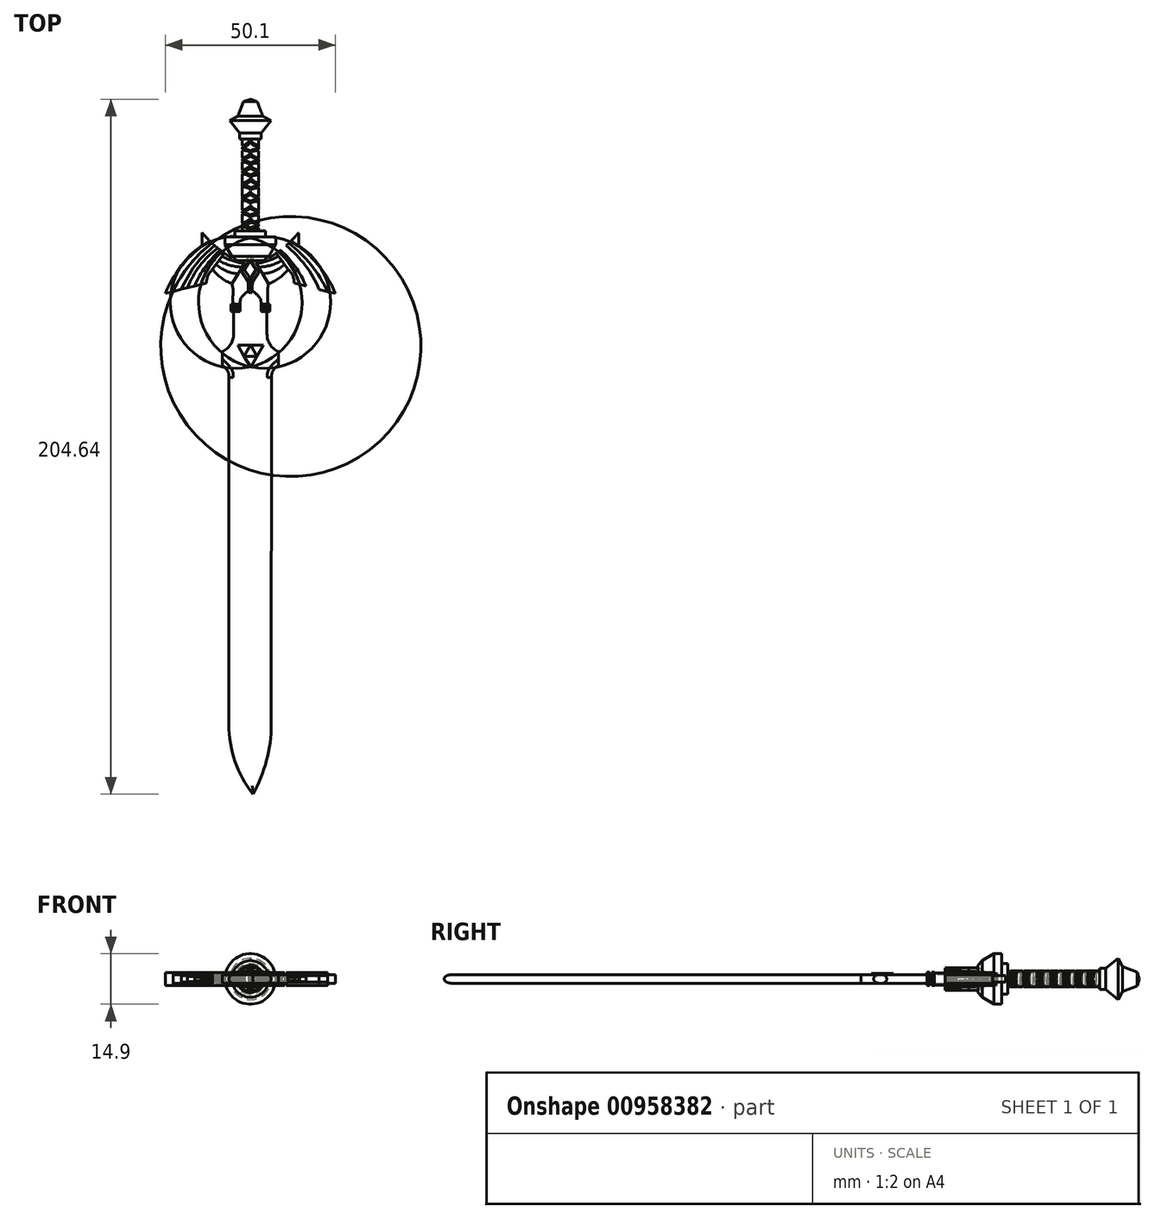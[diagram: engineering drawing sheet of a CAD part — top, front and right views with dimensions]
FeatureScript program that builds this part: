
annotation { "Feature Type Name" : "Feature", "Feature Type Description" : "" }
export const myFeature = defineFeature(function(context is Context, id is Id, definition is map)
    precondition{}
    {
        {
            var Q0;
            Q0=qCreatedBy(makeId("Top.planeOp"),FACE);
            var sketch = newSketch(context, id + "F0", { "sketchPlane" : qUnion([Q0])});
            skLineSegment(sketch, "E0", {"start": v(-5.22, 76.34) * mm, "end": v(-7.23, 75.61) * mm});
            skLineSegment(sketch, "E1", {"start": v(-7.23, 75.61) * mm, "end": v(-8.9, 71.32) * mm});
            skLineSegment(sketch, "E2", {"start": v(-8.9, 71.32) * mm, "end": v(-11.32, 70.05) * mm});
            skLineSegment(sketch, "E3", {"start": v(-11.32, 70.05) * mm, "end": v(-8.36, 66.38) * mm});
            skLineSegment(sketch, "E4", {"start": v(-8.36, 66.38) * mm, "end": v(-8.36, 64.56) * mm});
            skLineSegment(sketch, "E5", {"start": v(-8.36, 64.56) * mm, "end": v(-7.6, 64.56) * mm});
            skLineSegment(sketch, "E6", {"start": v(-7.6, 64.56) * mm, "end": v(-7.6, 37.58) * mm});
            skLineSegment(sketch, "E7", {"start": v(-7.6, 37.58) * mm, "end": v(-9.75, 37.58) * mm});
            skLineSegment(sketch, "E8", {"start": v(-9.75, 37.58) * mm, "end": v(-9.75, 35.78) * mm});
            skLineSegment(sketch, "E9", {"start": v(-9.75, 35.78) * mm, "end": v(-12.69, 35.78) * mm});
            skLineSegment(sketch, "E10", {"start": v(-12.69, 35.78) * mm, "end": v(-12.69, 33.54) * mm});
            skLineSegment(sketch, "E11", {"start": v(-12.69, 33.54) * mm, "end": v(-10.65, 30.07) * mm});
            skLineSegment(sketch, "E12", {"start": v(-10.65, 30.07) * mm, "end": v(-9.23, 28.83) * mm});
            skLineSegment(sketch, "E13", {"start": v(-9.23, 28.83) * mm, "end": v(-6.85, 28.22) * mm});
            skLineSegment(sketch, "E14", {"start": v(-6.85, 28.22) * mm, "end": v(-5.24, 30.4) * mm});
            skLineSegment(sketch, "E15", {"start": v(-5.24, 30.4) * mm, "end": v(-5.22, 76.34) * mm});
            skLineSegment(sketch, "E16", {"start": v(-10.65, 30.07) * mm, "end": v(-10.65, 29.62) * mm});
            skPoint(sketch, "E17.1.internal.snap0", {"position": v(-11.67, 31.8) * mm});
            skFitSpline(sketch, "E17", {"points": [v(-10.65, 29.62) * mm, v(-11.67, 30.16) * mm, v(-14.84, 32.47) * mm, v(-17.18, 34.56) * mm, v(-19.44, 37) * mm], "startDerivative": vector(-5.37, 2.5) * mm, "endDerivative": vector(-8.35, 9.25) * mm});
            skFitSpline(sketch, "E18", {"points": [v(-19.44, 37) * mm, v(-19.44, 35.95) * mm, v(-19.44, 33.83) * mm, v(-19.4, 33.07) * mm, v(-19.44, 33.1) * mm], "startDerivative": vector(0.06, -3.26) * mm, "endDerivative": vector(-1.19, 0.34) * mm});
            skArc(sketch, "E19", {"start": v(-19.4, 33.07) * mm, "mid": v(-25.78, 26.83) * mm, "end": v(-30.3, 19.12) * mm});
            skLineSegment(sketch, "E20", {"start": v(-30.3, 19.12) * mm, "end": v(-18.17, 22.24) * mm});
            skArc(sketch, "E21", {"start": v(-16.35, 26.26) * mm, "mid": v(-17.68, 24.44) * mm, "end": v(-18.17, 22.24) * mm});
            skArc(sketch, "E22", {"start": v(-16.35, 26.26) * mm, "mid": v(-13.8, 23.71) * mm, "end": v(-10.63, 21.98) * mm});
            skArc(sketch, "E23", {"start": v(-16.56, 33.95) * mm, "mid": v(-23.15, 27.52) * mm, "end": v(-28.02, 19.7) * mm});
            skArc(sketch, "E24", {"start": v(-15.75, 33.22) * mm, "mid": v(-21.45, 27.4) * mm, "end": v(-25.51, 20.35) * mm});
            skArc(sketch, "E25", {"start": v(-14.84, 32.47) * mm, "mid": v(-20.11, 27.25) * mm, "end": v(-23.78, 20.8) * mm});
            skArc(sketch, "E26", {"start": v(-14.1, 31.89) * mm, "mid": v(-18.47, 27.05) * mm, "end": v(-21.62, 21.35) * mm});
            skArc(sketch, "E27", {"start": v(-13.5, 31.43) * mm, "mid": v(-17.34, 27.1) * mm, "end": v(-19.75, 21.83) * mm});
            skLineSegment(sketch, "E28", {"start": v(-16.35, 26.26) * mm, "end": v(-12.92, 31) * mm});
            skLineSegment(sketch, "E29", {"start": v(-19.4, 33.07) * mm, "end": v(-17.18, 34.56) * mm});
            skArc(sketch, "E30", {"start": v(-15.35, 27.65) * mm, "mid": v(-12.5, 25.83) * mm, "end": v(-9.23, 24.95) * mm});
            skArc(sketch, "E31", {"start": v(-14.49, 28.83) * mm, "mid": v(-11.25, 27.44) * mm, "end": v(-7.76, 26.93) * mm});
            skArc(sketch, "E32", {"start": v(-13.57, 30.1) * mm, "mid": v(-10.47, 28.76) * mm, "end": v(-7.17, 28) * mm});
            skLineSegment(sketch, "E33", {"start": v(-6.85, 28.22) * mm, "end": v(-10.63, 21.98) * mm});
            skFitSpline(sketch, "E34", {"points": [v(-9.23, 24.95) * mm, v(-8.83, 24.95) * mm], "startDerivative": vector(0.4, 0) * mm, "endDerivative": vector(0.4, 0) * mm});
            skFitSpline(sketch, "E35", {"points": [v(-7.76, 26.93) * mm, v(-7.63, 26.93) * mm], "startDerivative": vector(0.13, 0) * mm, "endDerivative": vector(0.13, 0) * mm});
            skFitSpline(sketch, "E36", {"points": [v(-7.17, 28) * mm, v(-7, 27.99) * mm], "startDerivative": vector(0.17, -0.02) * mm, "endDerivative": vector(0.17, -0.02) * mm});
            skFitSpline(sketch, "E37.MirrorCS", {"points": [v(8.96, 36.98) * mm, v(8.96, 35.93) * mm, v(8.96, 33.81) * mm, v(8.9, 33.06) * mm, v(8.96, 33.08) * mm], "startDerivative": vector(-0.07, -3.26) * mm, "endDerivative": vector(1.19, 0.34) * mm});
            skLineSegment(sketch, "E38.MirrorCS", {"start": v(8.9, 33.06) * mm, "end": v(6.7, 34.54) * mm});
            skLineSegment(sketch, "E39.MirrorCS", {"start": v(5.86, 26.25) * mm, "end": v(2.43, 31) * mm});
            skLineSegment(sketch, "E40.MirrorCS", {"start": v(2.2, 35.77) * mm, "end": v(2.2, 33.53) * mm});
            skPoint(sketch, "E41.MirrorP", {"position": v(1.18, 31.8) * mm});
            skArc(sketch, "E42.MirrorCS", {"start": v(3.62, 31.88) * mm, "mid": v(7.97, 27.04) * mm, "end": v(11.12, 21.33) * mm});
            skArc(sketch, "E43.MirrorCS", {"start": v(5.27, 33.2) * mm, "mid": v(10.96, 27.4) * mm, "end": v(15.01, 20.33) * mm});
            skArc(sketch, "E44.MirrorCS", {"start": v(5.86, 26.25) * mm, "mid": v(7.18, 24.42) * mm, "end": v(7.67, 22.22) * mm});
            skArc(sketch, "E45.MirrorCS", {"start": v(4.36, 32.46) * mm, "mid": v(9.62, 27.23) * mm, "end": v(13.28, 20.78) * mm});
            skArc(sketch, "E46.MirrorCS", {"start": v(3, 31.42) * mm, "mid": v(6.85, 27.09) * mm, "end": v(9.25, 21.82) * mm});
            skLineSegment(sketch, "E47.MirrorCS", {"start": v(0.16, 30.07) * mm, "end": v(0.16, 29.61) * mm});
            skFitSpline(sketch, "E48.MirrorCS", {"points": [v(0.16, 29.61) * mm, v(1.18, 30.15) * mm, v(4.36, 32.46) * mm, v(6.7, 34.54) * mm, v(8.96, 36.98) * mm], "startDerivative": vector(5.37, 2.5) * mm, "endDerivative": vector(8.36, 9.24) * mm});
            skLineSegment(sketch, "E49.MirrorCS", {"start": v(2.2, 33.53) * mm, "end": v(0.16, 30.07) * mm});
            skArc(sketch, "E50.MirrorCS", {"start": v(5.86, 26.25) * mm, "mid": v(3.3, 23.7) * mm, "end": v(0.14, 21.97) * mm});
            skArc(sketch, "E51.MirrorCS", {"start": v(6.07, 33.93) * mm, "mid": v(12.66, 27.5) * mm, "end": v(17.52, 19.68) * mm});
            skArc(sketch, "E52.MirrorCS", {"start": v(8.9, 33.06) * mm, "mid": v(15.29, 26.8) * mm, "end": v(19.8, 19.1) * mm});
            skLineSegment(sketch, "E53.MirrorCS", {"start": v(19.8, 19.1) * mm, "end": v(7.67, 22.22) * mm});
            skFitSpline(sketch, "E54.MirrorCS", {"points": [v(0.16, 29.61) * mm, v(1.18, 30.15) * mm, v(4.36, 32.46) * mm, v(6.7, 34.54) * mm, v(8.96, 36.98) * mm], "startDerivative": vector(5.37, 2.5) * mm, "endDerivative": vector(8.36, 9.24) * mm});
            skArc(sketch, "E55.MirrorCS", {"start": v(4.86, 27.64) * mm, "mid": v(2, 25.82) * mm, "end": v(-1.27, 24.95) * mm});
            skArc(sketch, "E56.MirrorCS", {"start": v(4, 28.82) * mm, "mid": v(0.76, 27.43) * mm, "end": v(-2.73, 26.93) * mm});
            skArc(sketch, "E57.MirrorCS", {"start": v(3.08, 30.1) * mm, "mid": v(-0.02, 28.75) * mm, "end": v(-3.32, 28) * mm});
            skLineSegment(sketch, "E58.MirrorCS", {"start": v(-3.64, 28.22) * mm, "end": v(0.14, 21.97) * mm});
            skLineSegment(sketch, "E59.MirrorCS", {"start": v(0.16, 30.07) * mm, "end": v(-1.26, 28.83) * mm});
            skLineSegment(sketch, "E60.MirrorCS", {"start": v(-1.26, 28.83) * mm, "end": v(-3.64, 28.22) * mm});
            skFitSpline(sketch, "E61.MirrorCS", {"points": [v(-3.32, 28) * mm, v(-3.5, 27.99) * mm], "startDerivative": vector(-0.17, -0.02) * mm, "endDerivative": vector(-0.17, -0.02) * mm});
            skFitSpline(sketch, "E62.MirrorCS", {"points": [v(-2.73, 26.93) * mm, v(-2.86, 26.93) * mm], "startDerivative": vector(-0.13, 0) * mm, "endDerivative": vector(-0.13, 0) * mm});
            skFitSpline(sketch, "E63.MirrorCS", {"points": [v(-1.27, 24.95) * mm, v(-1.66, 24.95) * mm], "startDerivative": vector(-0.4, 0) * mm, "endDerivative": vector(-0.4, 0) * mm});
            skFitSpline(sketch, "E64", {"points": [v(-10.63, 21.98) * mm, v(-10.33, 20.1) * mm, v(-10.37, 18.46) * mm, v(-10.37, 16.67) * mm, v(-10.36, 15.95) * mm], "startDerivative": vector(1.43, -6.77) * mm, "endDerivative": vector(0.02, -3.56) * mm});
            skLineSegment(sketch, "E65", {"start": v(-10.36, 15.95) * mm, "end": v(-8.26, 15.95) * mm});
            skFitSpline(sketch, "E66", {"points": [v(-8.26, 15.95) * mm, v(-8.26, 16.44) * mm, v(-8.13, 17.45) * mm, v(-7.66, 18.2) * mm, v(-6.66, 19.28) * mm, v(-6, 19.75) * mm, v(-5.8, 19.83) * mm], "startDerivative": vector(-0.06, 3.2) * mm, "endDerivative": vector(1.98, 0.65) * mm});
            skFitSpline(sketch, "E67", {"points": [v(-4.62, 19.83) * mm, v(-3.94, 19.37) * mm, v(-3.02, 18.52) * mm, v(-2.42, 17.82) * mm, v(-2.16, 17.16) * mm, v(-2.1, 16.47) * mm, v(-2.1, 15.95) * mm], "startDerivative": vector(3.91, -2.38) * mm, "endDerivative": vector(0.1, -3.68) * mm});
            skLineSegment(sketch, "E68", {"start": v(-2.1, 15.95) * mm, "end": v(-0.16, 15.95) * mm});
            skFitSpline(sketch, "E69.MirrorCS", {"points": [v(0.14, 21.97) * mm, v(-0.17, 20.1) * mm, v(-0.13, 18.46) * mm, v(-0.13, 16.66) * mm, v(-0.14, 15.95) * mm], "startDerivative": vector(-1.44, -6.76) * mm, "endDerivative": vector(-0.02, -3.56) * mm});
            skLineSegment(sketch, "E70", {"start": v(-0.16, 15.95) * mm, "end": v(-0.14, 15.95) * mm});
            skLineSegment(sketch, "E71", {"start": v(-3.64, 28.22) * mm, "end": v(-5.24, 30.4) * mm});
            skLineSegment(sketch, "E72", {"start": v(-8.15, 26.08) * mm, "end": v(-5.86, 22.58) * mm});
            skLineSegment(sketch, "E73", {"start": v(-5.86, 22.58) * mm, "end": v(-5.8, 19.83) * mm});
            skLineSegment(sketch, "E74.MirrorCS", {"start": v(-2.34, 26.08) * mm, "end": v(-4.63, 22.58) * mm});
            skLineSegment(sketch, "E75.MirrorCS", {"start": v(-4.63, 22.58) * mm, "end": v(-4.7, 19.83) * mm});
            skLineSegment(sketch, "E76", {"start": v(-4.7, 19.83) * mm, "end": v(-4.62, 19.83) * mm});
            skLineSegment(sketch, "E77", {"start": v(-10.36, 15.95) * mm, "end": v(-10.95, 15.95) * mm});
            skLineSegment(sketch, "E78", {"start": v(-10.95, 15.95) * mm, "end": v(-10.95, 13.83) * mm});
            skLineSegment(sketch, "E79", {"start": v(-10.95, 13.83) * mm, "end": v(-8.63, 13.83) * mm});
            skLineSegment(sketch, "E80", {"start": v(-8.63, 13.83) * mm, "end": v(-8.27, 13.83) * mm});
            skLineSegment(sketch, "E81", {"start": v(-8.27, 13.83) * mm, "end": v(-8.26, 15.95) * mm});
            skLineSegment(sketch, "E82", {"start": v(-2.1, 15.95) * mm, "end": v(-2.1, 13.83) * mm});
            skLineSegment(sketch, "E83", {"start": v(-2.1, 13.83) * mm, "end": v(0.52, 13.83) * mm});
            skLineSegment(sketch, "E84", {"start": v(0.52, 13.83) * mm, "end": v(0.52, 15.95) * mm});
            skLineSegment(sketch, "E85", {"start": v(0.52, 15.95) * mm, "end": v(-0.16, 15.95) * mm});
            skLineSegment(sketch, "E86", {"start": v(-10.95, 15.26) * mm, "end": v(-8.26, 15.26) * mm});
            skLineSegment(sketch, "E87", {"start": v(-10.95, 14.53) * mm, "end": v(-8.26, 14.53) * mm});
            skLineSegment(sketch, "E88", {"start": v(-2.1, 15.22) * mm, "end": v(0.52, 15.22) * mm});
            skLineSegment(sketch, "E89", {"start": v(-2.1, 14.56) * mm, "end": v(0.52, 14.56) * mm});
            skLineSegment(sketch, "E90", {"start": v(-10.16, 13.83) * mm, "end": v(-10.16, 7.22) * mm});
            skArc(sketch, "E91", {"start": v(-13.54, 1.97) * mm, "mid": v(-11.08, 4.1) * mm, "end": v(-10.16, 7.22) * mm});
            skLineSegment(sketch, "E92", {"start": v(-13.54, 1.97) * mm, "end": v(-13.54, -1.9) * mm});
            skFitSpline(sketch, "E93", {"points": [v(-13.54, -1.9) * mm, v(-12.3, -3.14) * mm, v(-11.8, -3.88) * mm, v(-11.55, -4.81) * mm, v(-11.55, -5.66) * mm], "startDerivative": vector(4.34, -4.17) * mm, "endDerivative": vector(-0.22, -3.77) * mm});
            skLineSegment(sketch, "E94", {"start": v(-11.55, -5.66) * mm, "end": v(-11.55, -107.82) * mm});
            skLineSegment(sketch, "E95.MirrorCS", {"start": v(1.02, -5.67) * mm, "end": v(0.91, -107.82) * mm});
            skLineSegment(sketch, "E96.MirrorCS", {"start": v(-0.34, 13.83) * mm, "end": v(-0.35, 7.21) * mm});
            skArc(sketch, "E97.MirrorCS", {"start": v(3.03, 1.96) * mm, "mid": v(0.56, 4.1) * mm, "end": v(-0.35, 7.21) * mm});
            skLineSegment(sketch, "E98.MirrorCS", {"start": v(3.03, 1.96) * mm, "end": v(3.02, -1.91) * mm});
            skFitSpline(sketch, "E99.MirrorCS", {"points": [v(3.02, -1.91) * mm, v(1.78, -3.15) * mm, v(1.28, -3.9) * mm, v(1.02, -4.82) * mm, v(1.02, -5.67) * mm], "startDerivative": vector(-4.35, -4.17) * mm, "endDerivative": vector(0.22, -3.77) * mm});
            skArc(sketch, "E100", {"start": v(-11.55, -107.82) * mm, "mid": v(-9.73, -118.65) * mm, "end": v(-4.5, -128.3) * mm});
            skArc(sketch, "E101", {"start": v(-4.5, -128.3) * mm, "mid": v(-0.47, -118.4) * mm, "end": v(0.91, -107.82) * mm});
            skLineSegment(sketch, "E102", {"start": v(-4.7, 19.83) * mm, "end": v(-5.24, 19.13) * mm});
            skLineSegment(sketch, "E103", {"start": v(-5.24, 19.13) * mm, "end": v(-5.8, 19.83) * mm});
            skLineSegment(sketch, "E104", {"start": v(-0.34, 13.83) * mm, "end": v(-0.34, 13.83) * mm});
            skSolve(sketch);
        }
        {
            var Q0;
            Q0=makeQuery(id+"F0.imprint","IMPRINT",FACE,{"disambiguationData":[TD([[makeQuery(id+"F0.imprint","IMPRINT",EDGE,{"derivedFrom":sQuery(id+"F0.wireOp",EDGE,"E0")}),1.0]])]});
            var Q1;
            Q1=sQuery(id+"F0.wireOp",EDGE,"E15");
            revolve(context, id + "F1", {"surfaceOperationType" : NewSurfaceOperationType.NEW, "entities" : qUnion([Q0]), "axis" : qUnion([Q1]), "revolveType" : RevolveType.FULL});
        }
        {
            var Q0;
            {var subQ1=sQuery(id+"F0.wireOp",EDGE,"E22");Q0=makeQuery(id+"F0.imprint","IMPRINT",FACE,{"disambiguationData":[TD([[makeQuery(id+"F0.imprint","IMPRINT",EDGE,{"derivedFrom":subQ1}),1.0]])]});}
            var Q1;
            {var subQ2=sQuery(id+"F0.wireOp",EDGE,"E19");Q1=makeQuery(id+"F0.imprint","IMPRINT",FACE,{"disambiguationData":[TD([[makeQuery(id+"F0.imprint","IMPRINT",EDGE,{"derivedFrom":subQ2}),1.0]])]});}
            var Q2;
            {var subQ3=sQuery(id+"F0.wireOp",EDGE,"E55.MirrorCS");Q2=makeQuery(id+"F0.imprint","IMPRINT",FACE,{"disambiguationData":[TD([[makeQuery(id+"F0.imprint","IMPRINT",EDGE,{"derivedFrom":subQ3}),1.0]])]});}
            var Q3;
            {var subQ5=sQuery(id+"F0.wireOp",EDGE,"E51.MirrorCS");Q3=makeQuery(id+"F0.imprint","IMPRINT",FACE,{"disambiguationData":[TD([[makeQuery(id+"F0.imprint","IMPRINT",EDGE,{"derivedFrom":subQ5}),1.0]])]});}
            extrude(context, id + "F2", {"entities" : qUnion([Q0, Q1, Q2, Q3]), "endBound" : BoundingType.SYMMETRIC, "depth" : 3.86 * mm, "offsetDistance" : 25.4 * mm});
        }
        {
            var Q0;
            {var subQ0=sQuery(id+"F0.wireOp",EDGE,"E23");Q0=makeQuery(id+"F0.imprint","IMPRINT",FACE,{"disambiguationData":[TD([[makeQuery(id+"F0.imprint","IMPRINT",EDGE,{"derivedFrom":subQ0}),1.0]])]});}
            var Q1;
            {var subQ4=sQuery(id+"F0.wireOp",EDGE,"E30");Q1=makeQuery(id+"F0.imprint","IMPRINT",FACE,{"disambiguationData":[TD([[makeQuery(id+"F0.imprint","IMPRINT",EDGE,{"derivedFrom":subQ4}),1.0]])]});}
            var Q2;
            {var subQ3=sQuery(id+"F0.wireOp",EDGE,"E55.MirrorCS");Q2=makeQuery(id+"F0.imprint","IMPRINT",FACE,{"disambiguationData":[TD([[makeQuery(id+"F0.imprint","IMPRINT",EDGE,{"derivedFrom":subQ3}),-1.0]])]});}
            var Q3;
            {var subQ0=sQuery(id+"F0.wireOp",EDGE,"E51.MirrorCS");Q3=makeQuery(id+"F0.imprint","IMPRINT",FACE,{"disambiguationData":[TD([[makeQuery(id+"F0.imprint","IMPRINT",EDGE,{"derivedFrom":subQ0}),-1.0]])]});}
            extrude(context, id + "F3", {"entities" : qUnion([Q0, Q1, Q2, Q3]), "endBound" : BoundingType.SYMMETRIC, "depth" : 2.54 * mm, "offsetDistance" : 25.4 * mm});
        }
        {
            var Q0;
            {var subQ0=sQuery(id+"F0.wireOp",EDGE,"E24");Q0=makeQuery(id+"F0.imprint","IMPRINT",FACE,{"disambiguationData":[TD([[makeQuery(id+"F0.imprint","IMPRINT",EDGE,{"derivedFrom":subQ0}),1.0]])]});}
            var Q1;
            {var subQ4=sQuery(id+"F0.wireOp",EDGE,"E31");Q1=makeQuery(id+"F0.imprint","IMPRINT",FACE,{"disambiguationData":[TD([[makeQuery(id+"F0.imprint","IMPRINT",EDGE,{"derivedFrom":subQ4}),1.0]])]});}
            var Q2;
            {var subQ0=sQuery(id+"F0.wireOp",EDGE,"E43.MirrorCS");Q2=makeQuery(id+"F0.imprint","IMPRINT",FACE,{"disambiguationData":[TD([[makeQuery(id+"F0.imprint","IMPRINT",EDGE,{"derivedFrom":subQ0}),-1.0]])]});}
            var Q3;
            {var subQ3=sQuery(id+"F0.wireOp",EDGE,"E56.MirrorCS");Q3=makeQuery(id+"F0.imprint","IMPRINT",FACE,{"disambiguationData":[TD([[makeQuery(id+"F0.imprint","IMPRINT",EDGE,{"derivedFrom":subQ3}),-1.0]])]});}
            extrude(context, id + "F4", {"entities" : qUnion([Q0, Q1, Q2, Q3]), "endBound" : BoundingType.SYMMETRIC, "depth" : 1.93 * mm, "offsetDistance" : 25.4 * mm});
        }
        {
            var Q0;
            Q0=makeQuery(id+"F0.imprint","IMPRINT",FACE,{"disambiguationData":[TD([[makeQuery(id+"F0.imprint","IMPRINT",EDGE,{"derivedFrom":sQuery(id+"F0.wireOp",EDGE,"E12")}),-1.0]])]});
            var Q1;
            {var subQ0=sQuery(id+"F0.wireOp",EDGE,"E25");Q1=makeQuery(id+"F0.imprint","IMPRINT",FACE,{"disambiguationData":[TD([[makeQuery(id+"F0.imprint","IMPRINT",EDGE,{"derivedFrom":subQ0}),1.0]])]});}
            var Q2;
            {var subQ2=sQuery(id+"F0.wireOp",EDGE,"E47.MirrorCS");Q2=makeQuery(id+"F0.imprint","IMPRINT",FACE,{"disambiguationData":[TD([[makeQuery(id+"F0.imprint","IMPRINT",EDGE,{"derivedFrom":subQ2}),-1.0]])]});}
            var Q3;
            {var subQ0=sQuery(id+"F0.wireOp",EDGE,"E42.MirrorCS");Q3=makeQuery(id+"F0.imprint","IMPRINT",FACE,{"disambiguationData":[TD([[makeQuery(id+"F0.imprint","IMPRINT",EDGE,{"derivedFrom":subQ0}),1.0]])]});}
            extrude(context, id + "F5", {"entities" : qUnion([Q0, Q1, Q2, Q3]), "endBound" : BoundingType.SYMMETRIC, "depth" : 1.47 * mm, "offsetDistance" : 25.4 * mm});
        }
        {
            var Q0;
            {var subQ0=sQuery(id+"F0.wireOp",EDGE,"E46.MirrorCS");Q0=makeQuery(id+"F0.imprint","IMPRINT",FACE,{"disambiguationData":[TD([[makeQuery(id+"F0.imprint","IMPRINT",EDGE,{"derivedFrom":subQ0}),1.0]])]});}
            var Q1;
            {var subQ0=sQuery(id+"F0.wireOp",EDGE,"E26");Q1=makeQuery(id+"F0.imprint","IMPRINT",FACE,{"disambiguationData":[TD([[makeQuery(id+"F0.imprint","IMPRINT",EDGE,{"derivedFrom":subQ0}),1.0]])]});}
            extrude(context, id + "F6", {"entities" : qUnion([Q0, Q1]), "endBound" : BoundingType.SYMMETRIC, "oppositeDirection" : true, "depth" : 1.02 * mm, "offsetDistance" : 25.4 * mm});
        }
        {
            var Q0;
            {var subQ6=sQuery(id+"F0.wireOp",EDGE,"E44.MirrorCS");Q0=makeQuery(id+"F0.imprint","IMPRINT",FACE,{"disambiguationData":[TD([[makeQuery(id+"F0.imprint","IMPRINT",EDGE,{"derivedFrom":subQ6}),1.0]])]});}
            var Q1;
            {var subQ1=sQuery(id+"F0.wireOp",EDGE,"E21");Q1=makeQuery(id+"F0.imprint","IMPRINT",FACE,{"disambiguationData":[TD([[makeQuery(id+"F0.imprint","IMPRINT",EDGE,{"derivedFrom":subQ1}),-1.0]])]});}
            extrude(context, id + "F7", {"entities" : qUnion([Q0, Q1]), "endBound" : BoundingType.SYMMETRIC, "depth" : 0.76 * mm, "offsetDistance" : 25.4 * mm});
        }
        {
            var Q0;
            {var subQ6=sQuery(id+"F0.wireOp",EDGE,"E14");Q0=makeQuery(id+"F0.imprint","IMPRINT",FACE,{"disambiguationData":[TD([[makeQuery(id+"F0.imprint","IMPRINT",EDGE,{"derivedFrom":subQ6}),-1.0]])]});}
            extrude(context, id + "F8", {"entities" : qUnion([Q0]), "endBound" : BoundingType.SYMMETRIC, "depth" : 6.6 * mm, "offsetDistance" : 25.4 * mm});
        }
        {
            var Q0;
            Q0=makeQuery(id+"F0.imprint","IMPRINT",FACE,{"disambiguationData":[TD([[makeQuery(id+"F0.imprint","IMPRINT",EDGE,{"derivedFrom":sQuery(id+"F0.wireOp",EDGE,"E67")}),1.0]])]});
            var Q1;
            {var subQ0=sQuery(id+"F0.wireOp",EDGE,"E64");Q1=makeQuery(id+"F0.imprint","IMPRINT",FACE,{"disambiguationData":[TD([[makeQuery(id+"F0.imprint","IMPRINT",EDGE,{"derivedFrom":subQ0}),1.0]])]});}
            extrude(context, id + "F9", {"entities" : qUnion([Q0, Q1]), "endBound" : BoundingType.SYMMETRIC, "depth" : 3.56 * mm, "offsetDistance" : 25.4 * mm});
        }
        {
            var Q0;
            Q0=makeQuery(id+"F8.opExtrude","CAP_EDGE",EDGE,{"disambiguationData":[OSD([sQuery(id+"F0.wireOp",EDGE,"E33")])],"isStart":false});
            var Q1;
            Q1=makeQuery(id+"F8.opExtrude","CAP_EDGE",EDGE,{"disambiguationData":[OSD([sQuery(id+"F0.wireOp",EDGE,"E58.MirrorCS")])],"isStart":false});
            var Q2;
            Q2=makeQuery(id+"F8.opExtrude","CAP_EDGE",EDGE,{"disambiguationData":[OSD([sQuery(id+"F0.wireOp",EDGE,"E72")])],"isStart":false});
            var Q3;
            Q3=makeQuery(id+"F8.opExtrude","CAP_EDGE",EDGE,{"disambiguationData":[OSD([sQuery(id+"F0.wireOp",EDGE,"E74.MirrorCS")])],"isStart":false});
            var Q4;
            Q4=makeQuery(id+"F8.opExtrude","CAP_EDGE",EDGE,{"disambiguationData":[OSD([sQuery(id+"F0.wireOp",EDGE,"E72")])],"isStart":true});
            var Q5;
            Q5=makeQuery(id+"F8.opExtrude","CAP_EDGE",EDGE,{"disambiguationData":[OSD([sQuery(id+"F0.wireOp",EDGE,"E33")])],"isStart":true});
            var Q6;
            Q6=makeQuery(id+"F8.opExtrude","CAP_EDGE",EDGE,{"disambiguationData":[OSD([sQuery(id+"F0.wireOp",EDGE,"E58.MirrorCS")])],"isStart":true});
            var Q7;
            Q7=makeQuery(id+"F8.opExtrude","CAP_EDGE",EDGE,{"disambiguationData":[OSD([sQuery(id+"F0.wireOp",EDGE,"E74.MirrorCS")])],"isStart":true});
            chamfer(context, id + "F10", {"entities" : qUnion([Q0, Q1, Q2, Q3, Q4, Q5, Q6, Q7]), "width" : 1.02 * mm, "tangentPropagation" : true});
        }
        {
            var Q0;
            Q0=makeQuery(id+"F8.opExtrude","CAP_EDGE",EDGE,{"disambiguationData":[OSD([sQuery(id+"F0.wireOp",EDGE,"E73")])],"isStart":false});
            var Q1;
            Q1=makeQuery(id+"F8.opExtrude","CAP_EDGE",EDGE,{"disambiguationData":[OSD([sQuery(id+"F0.wireOp",EDGE,"E75.MirrorCS")])],"isStart":false});
            var Q2;
            Q2=makeQuery(id+"F8.opExtrude","CAP_EDGE",EDGE,{"disambiguationData":[OSD([sQuery(id+"F0.wireOp",EDGE,"E73")])],"isStart":true});
            var Q3;
            Q3=makeQuery(id+"F8.opExtrude","CAP_EDGE",EDGE,{"disambiguationData":[OSD([sQuery(id+"F0.wireOp",EDGE,"E75.MirrorCS")])],"isStart":true});
            chamfer(context, id + "F11", {"entities" : qUnion([Q0, Q1, Q2, Q3]), "width" : 0.5 * mm, "tangentPropagation" : true});
        }
        {
            var Q0;
            {var subQ1=sQuery(id+"F0.wireOp",EDGE,"E65");Q0=makeQuery(id+"F0.imprint","IMPRINT",FACE,{"disambiguationData":[TD([[makeQuery(id+"F0.imprint","IMPRINT",EDGE,{"derivedFrom":subQ1}),-1.0]])]});}
            var Q1;
            {var subQ5=sQuery(id+"F0.wireOp",EDGE,"E68");Q1=makeQuery(id+"F0.imprint","IMPRINT",FACE,{"disambiguationData":[TD([[makeQuery(id+"F0.imprint","IMPRINT",EDGE,{"derivedFrom":subQ5}),-1.0]])]});}
            var Q2;
            {var subQ0=sQuery(id+"F0.wireOp",EDGE,"E80");Q2=makeQuery(id+"F0.imprint","IMPRINT",FACE,{"disambiguationData":[TD([[makeQuery(id+"F0.imprint","IMPRINT",EDGE,{"derivedFrom":subQ0}),1.0]])]});}
            var Q3;
            {var subQ0=sQuery(id+"F0.wireOp",EDGE,"E83");Q3=makeQuery(id+"F0.imprint","IMPRINT",FACE,{"disambiguationData":[TD([[makeQuery(id+"F0.imprint","IMPRINT",EDGE,{"derivedFrom":subQ0}),1.0]])]});}
            extrude(context, id + "F12", {"entities" : qUnion([Q0, Q1, Q2, Q3]), "endBound" : BoundingType.SYMMETRIC, "depth" : 3.91 * mm, "offsetDistance" : 25.4 * mm});
        }
        {
            var Q0;
            {var subQ0=sQuery(id+"F0.wireOp",EDGE,"E86");Q0=makeQuery(id+"F0.imprint","IMPRINT",FACE,{"disambiguationData":[TD([[makeQuery(id+"F0.imprint","IMPRINT",EDGE,{"derivedFrom":subQ0}),-1.0]])]});}
            var Q1;
            {var subQ0=sQuery(id+"F0.wireOp",EDGE,"E88");Q1=makeQuery(id+"F0.imprint","IMPRINT",FACE,{"disambiguationData":[TD([[makeQuery(id+"F0.imprint","IMPRINT",EDGE,{"derivedFrom":subQ0}),-1.0]])]});}
            extrude(context, id + "F13", {"entities" : qUnion([Q0, Q1]), "endBound" : BoundingType.SYMMETRIC, "depth" : 3.15 * mm, "offsetDistance" : 25.4 * mm});
        }
        {
            var Q0;
            {var subQ10=sQuery(id+"F0.wireOp",EDGE,"E66");Q0=makeQuery(id+"F0.imprint","IMPRINT",FACE,{"disambiguationData":[TD([[makeQuery(id+"F0.imprint","IMPRINT",EDGE,{"derivedFrom":subQ10}),-1.0]])]});}
            extrude(context, id + "F14", {"entities" : qUnion([Q0]), "endBound" : BoundingType.SYMMETRIC, "depth" : 2.54 * mm, "offsetDistance" : 25.4 * mm});
        }
        {
            var Q0;
            Q0=makeQuery(id+"F14.opExtrude","CAP_EDGE",EDGE,{"disambiguationData":[OSD([sQuery(id+"F0.wireOp",EDGE,"E96.MirrorCS")])],"isStart":false});
            var Q1;
            Q1=makeQuery(id+"F14.opExtrude","CAP_EDGE",EDGE,{"disambiguationData":[OSD([sQuery(id+"F0.wireOp",EDGE,"E90")])],"isStart":false});
            var Q2;
            Q2=makeQuery(id+"F14.opExtrude","CAP_EDGE",EDGE,{"disambiguationData":[OSD([sQuery(id+"F0.wireOp",EDGE,"E95.MirrorCS")])],"isStart":false});
            var Q3;
            Q3=makeQuery(id+"F14.opExtrude","CAP_EDGE",EDGE,{"disambiguationData":[OSD([sQuery(id+"F0.wireOp",EDGE,"E94")])],"isStart":false});
            fillet(context, id + "F15", {"entities" : qUnion([Q0, Q1, Q2, Q3]), "radius" : 1.27 * mm, "tangentPropagation" : true, "allowEdgeOverflow" : false});
        }
        {
            var Q0;
            Q0=makeQuery(id+"F14.opExtrude","CAP_EDGE",EDGE,{"disambiguationData":[OSD([sQuery(id+"F0.wireOp",EDGE,"E101")])],"isStart":true});
            var Q1;
            Q1=makeQuery(id+"F14.opExtrude","CAP_EDGE",EDGE,{"disambiguationData":[OSD([sQuery(id+"F0.wireOp",EDGE,"E100")])],"isStart":true});
            var Q2;
            Q2=makeQuery(id+"F14.opExtrude","CAP_EDGE",EDGE,{"disambiguationData":[OSD([sQuery(id+"F0.wireOp",EDGE,"E95.MirrorCS")])],"isStart":true});
            var Q3;
            Q3=makeQuery(id+"F14.opExtrude","CAP_EDGE",EDGE,{"disambiguationData":[OSD([sQuery(id+"F0.wireOp",EDGE,"E94")])],"isStart":true});
            var Q4;
            Q4=makeQuery(id+"F14.opExtrude","CAP_EDGE",EDGE,{"disambiguationData":[OSD([sQuery(id+"F0.wireOp",EDGE,"E91")])],"isStart":true});
            var Q5;
            Q5=makeQuery(id+"F14.opExtrude","CAP_EDGE",EDGE,{"disambiguationData":[OSD([sQuery(id+"F0.wireOp",EDGE,"E97.MirrorCS")])],"isStart":true});
            fillet(context, id + "F16", {"entities" : qUnion([Q0, Q1, Q2, Q3, Q4, Q5]), "radius" : 1.27 * mm, "tangentPropagation" : true, "allowEdgeOverflow" : false});
        }
        {
            var Q0;
            {var subQ0=sQuery(id+"F0.wireOp",EDGE,"E18");var subQ1=sQuery(id+"F0.wireOp",EDGE,"E17");var subQ2=makeQuery(id+"F0.imprint","INTERSECT",VERTEX,{"derivedFrom":[subQ1,subQ0]});Q0=makeQuery(id+"F0.imprint","IMPRINT",FACE,{"disambiguationData":[TD([[makeQuery(id+"F0.imprint","IMPRINT",EDGE,{"disambiguationData":[TD([[subQ2,1.0]])],"derivedFrom":subQ1}),1.0]])]});}
            var Q1;
            {var subQ0=sQuery(id+"F0.wireOp",EDGE,"E54.MirrorCS");var subQ1=sQuery(id+"F0.wireOp",EDGE,"E37.MirrorCS");var subQ2=makeQuery(id+"F0.imprint","INTERSECT",VERTEX,{"derivedFrom":[subQ1,subQ0]});Q1=makeQuery(id+"F0.imprint","IMPRINT",FACE,{"disambiguationData":[TD([[makeQuery(id+"F0.imprint","IMPRINT",EDGE,{"disambiguationData":[TD([[subQ2,-1.0]])],"derivedFrom":subQ1}),-1.0]])]});}
            extrude(context, id + "F17", {"entities" : qUnion([Q0, Q1]), "endBound" : BoundingType.SYMMETRIC, "depth" : 1.93 * mm, "offsetDistance" : 25.4 * mm});
        }
        {
            var Q0;
            Q0=qCreatedBy(makeId("Top.planeOp"),FACE);
            cPlane(context, id + "F18", {"entities" : qUnion([Q0]), "cplaneType" : CPlaneType.OFFSET, "offset" : 24.13 * mm, "width" : 152.4 * mm, "height" : 152.4 * mm});
        }
        {
            var Q0;
            Q0=qCreatedBy(id+"F18.planeOp",FACE);
            var sketch = newSketch(context, id + "F19", { "sketchPlane" : qUnion([Q0])});
            skArc(sketch, "E105", {"start": v(-7.6, 62.67) * mm, "mid": v(-6.27, 63.36) * mm, "end": v(-5.28, 64.5) * mm});
            skArc(sketch, "E106", {"start": v(-5.28, 64.5) * mm, "mid": v(-4.32, 63.35) * mm, "end": v(-2.9, 62.86) * mm});
            skArc(sketch, "E107", {"start": v(-7.64, 62.11) * mm, "mid": v(-6.32, 62.62) * mm, "end": v(-5.28, 63.57) * mm});
            skArc(sketch, "E108", {"start": v(-5.28, 63.57) * mm, "mid": v(-4.17, 62.68) * mm, "end": v(-2.83, 62.18) * mm});
            skArc(sketch, "E109", {"start": v(-5.28, 61.16) * mm, "mid": v(-6.44, 61.63) * mm, "end": v(-7.68, 61.7) * mm});
            skArc(sketch, "E110", {"start": v(-2.83, 61.57) * mm, "mid": v(-4.1, 61.58) * mm, "end": v(-5.28, 61.16) * mm});
            skArc(sketch, "E111", {"start": v(-5.25, 60.69) * mm, "mid": v(-6.41, 61.16) * mm, "end": v(-7.66, 61.22) * mm});
            skArc(sketch, "E112", {"start": v(-2.84, 61.09) * mm, "mid": v(-4.08, 61.09) * mm, "end": v(-5.25, 60.69) * mm});
            skArc(sketch, "E113", {"start": v(-7.66, 59.05) * mm, "mid": v(-6.33, 59.51) * mm, "end": v(-5.23, 60.4) * mm});
            skArc(sketch, "E114", {"start": v(-5.23, 60.4) * mm, "mid": v(-4.16, 59.48) * mm, "end": v(-2.83, 59.05) * mm});
            skArc(sketch, "E115", {"start": v(-7.66, 58.65) * mm, "mid": v(-6.37, 58.91) * mm, "end": v(-5.23, 59.56) * mm});
            skArc(sketch, "E116", {"start": v(-5.23, 59.56) * mm, "mid": v(-4.08, 58.91) * mm, "end": v(-2.8, 58.58) * mm});
            skArc(sketch, "E117", {"start": v(-5.23, 57.6) * mm, "mid": v(-6.38, 58.15) * mm, "end": v(-7.66, 58.24) * mm});
            skArc(sketch, "E118", {"start": v(-2.86, 58.1) * mm, "mid": v(-4.09, 58.04) * mm, "end": v(-5.23, 57.6) * mm});
            skArc(sketch, "E119", {"start": v(-5.23, 56.97) * mm, "mid": v(-6.37, 57.61) * mm, "end": v(-7.66, 57.86) * mm});
            skArc(sketch, "E120", {"start": v(-2.84, 57.54) * mm, "mid": v(-4.08, 57.45) * mm, "end": v(-5.23, 56.97) * mm});
            skLineSegment(sketch, "E121", {"start": v(-7.6, 62.67) * mm, "end": v(-7.64, 62.11) * mm});
            skLineSegment(sketch, "E122", {"start": v(-7.68, 61.7) * mm, "end": v(-7.66, 61.22) * mm});
            skLineSegment(sketch, "E123", {"start": v(-7.66, 59.05) * mm, "end": v(-7.66, 58.65) * mm});
            skLineSegment(sketch, "E124", {"start": v(-7.66, 58.24) * mm, "end": v(-7.66, 57.86) * mm});
            skLineSegment(sketch, "E125", {"start": v(-2.84, 57.54) * mm, "end": v(-2.86, 58.1) * mm});
            skLineSegment(sketch, "E126", {"start": v(-2.8, 58.58) * mm, "end": v(-2.83, 59.05) * mm});
            skLineSegment(sketch, "E127", {"start": v(-2.84, 61.09) * mm, "end": v(-2.83, 61.57) * mm});
            skLineSegment(sketch, "E128", {"start": v(-2.83, 62.18) * mm, "end": v(-2.9, 62.86) * mm});
            skArc(sketch, "E129", {"start": v(-7.68, 55.5) * mm, "mid": v(-6.34, 55.96) * mm, "end": v(-5.24, 56.84) * mm});
            skArc(sketch, "E130", {"start": v(-5.24, 56.84) * mm, "mid": v(-4.18, 55.93) * mm, "end": v(-2.85, 55.5) * mm});
            skArc(sketch, "E131", {"start": v(-7.68, 55.1) * mm, "mid": v(-6.39, 55.36) * mm, "end": v(-5.24, 56) * mm});
            skArc(sketch, "E132", {"start": v(-5.24, 56) * mm, "mid": v(-4.1, 55.36) * mm, "end": v(-2.82, 55.03) * mm});
            skArc(sketch, "E133", {"start": v(-5.24, 54.04) * mm, "mid": v(-6.4, 54.6) * mm, "end": v(-7.68, 54.68) * mm});
            skArc(sketch, "E134", {"start": v(-2.88, 54.54) * mm, "mid": v(-4.1, 54.5) * mm, "end": v(-5.24, 54.04) * mm});
            skArc(sketch, "E135", {"start": v(-5.24, 53.41) * mm, "mid": v(-6.39, 54.06) * mm, "end": v(-7.68, 54.3) * mm});
            skArc(sketch, "E136", {"start": v(-2.85, 53.99) * mm, "mid": v(-4.1, 53.9) * mm, "end": v(-5.24, 53.41) * mm});
            skLineSegment(sketch, "E137", {"start": v(-7.68, 55.5) * mm, "end": v(-7.68, 55.1) * mm});
            skLineSegment(sketch, "E138", {"start": v(-7.68, 54.68) * mm, "end": v(-7.68, 54.3) * mm});
            skLineSegment(sketch, "E139", {"start": v(-2.85, 53.99) * mm, "end": v(-2.88, 54.54) * mm});
            skLineSegment(sketch, "E140", {"start": v(-2.82, 55.03) * mm, "end": v(-2.85, 55.5) * mm});
            skArc(sketch, "E141", {"start": v(-7.55, 51.7) * mm, "mid": v(-6.22, 52.16) * mm, "end": v(-5.12, 53.04) * mm});
            skArc(sketch, "E142", {"start": v(-5.12, 53.04) * mm, "mid": v(-4.05, 52.13) * mm, "end": v(-2.72, 51.7) * mm});
            skArc(sketch, "E143", {"start": v(-7.55, 51.3) * mm, "mid": v(-6.26, 51.56) * mm, "end": v(-5.12, 52.2) * mm});
            skArc(sketch, "E144", {"start": v(-5.12, 52.2) * mm, "mid": v(-3.97, 51.56) * mm, "end": v(-2.7, 51.23) * mm});
            skArc(sketch, "E145", {"start": v(-5.12, 50.24) * mm, "mid": v(-6.27, 50.8) * mm, "end": v(-7.55, 50.89) * mm});
            skArc(sketch, "E146", {"start": v(-2.75, 50.74) * mm, "mid": v(-3.98, 50.7) * mm, "end": v(-5.12, 50.24) * mm});
            skArc(sketch, "E147", {"start": v(-5.12, 49.62) * mm, "mid": v(-6.26, 50.26) * mm, "end": v(-7.55, 50.5) * mm});
            skArc(sketch, "E148", {"start": v(-2.72, 50.19) * mm, "mid": v(-3.97, 50.1) * mm, "end": v(-5.12, 49.62) * mm});
            skLineSegment(sketch, "E149", {"start": v(-7.55, 51.7) * mm, "end": v(-7.55, 51.3) * mm});
            skLineSegment(sketch, "E150", {"start": v(-7.55, 50.89) * mm, "end": v(-7.55, 50.5) * mm});
            skLineSegment(sketch, "E151", {"start": v(-2.72, 50.19) * mm, "end": v(-2.75, 50.74) * mm});
            skLineSegment(sketch, "E152", {"start": v(-2.7, 51.23) * mm, "end": v(-2.72, 51.7) * mm});
            skArc(sketch, "E153", {"start": v(-7.7, 47.74) * mm, "mid": v(-6.37, 48.2) * mm, "end": v(-5.27, 49.1) * mm});
            skArc(sketch, "E154", {"start": v(-5.27, 49.1) * mm, "mid": v(-4.2, 48.18) * mm, "end": v(-2.87, 47.74) * mm});
            skArc(sketch, "E155", {"start": v(-7.7, 47.35) * mm, "mid": v(-6.41, 47.61) * mm, "end": v(-5.27, 48.25) * mm});
            skArc(sketch, "E156", {"start": v(-5.27, 48.25) * mm, "mid": v(-4.12, 47.61) * mm, "end": v(-2.85, 47.28) * mm});
            skArc(sketch, "E157", {"start": v(-5.27, 46.29) * mm, "mid": v(-6.42, 46.85) * mm, "end": v(-7.7, 46.94) * mm});
            skArc(sketch, "E158", {"start": v(-2.9, 46.8) * mm, "mid": v(-4.13, 46.74) * mm, "end": v(-5.27, 46.29) * mm});
            skArc(sketch, "E159", {"start": v(-5.27, 45.67) * mm, "mid": v(-6.41, 46.3) * mm, "end": v(-7.7, 46.55) * mm});
            skArc(sketch, "E160", {"start": v(-2.88, 46.24) * mm, "mid": v(-4.12, 46.15) * mm, "end": v(-5.27, 45.67) * mm});
            skLineSegment(sketch, "E161", {"start": v(-7.7, 47.74) * mm, "end": v(-7.7, 47.35) * mm});
            skLineSegment(sketch, "E162", {"start": v(-7.7, 46.94) * mm, "end": v(-7.7, 46.55) * mm});
            skLineSegment(sketch, "E163", {"start": v(-2.88, 46.24) * mm, "end": v(-2.9, 46.8) * mm});
            skLineSegment(sketch, "E164", {"start": v(-2.85, 47.28) * mm, "end": v(-2.87, 47.74) * mm});
            skArc(sketch, "E165", {"start": v(-7.65, 43.68) * mm, "mid": v(-6.32, 44.14) * mm, "end": v(-5.22, 45.03) * mm});
            skArc(sketch, "E166", {"start": v(-5.22, 45.03) * mm, "mid": v(-4.15, 44.12) * mm, "end": v(-2.82, 43.68) * mm});
            skArc(sketch, "E167", {"start": v(-7.65, 43.28) * mm, "mid": v(-6.36, 43.55) * mm, "end": v(-5.22, 44.2) * mm});
            skArc(sketch, "E168", {"start": v(-5.22, 44.2) * mm, "mid": v(-4.07, 43.55) * mm, "end": v(-2.8, 43.21) * mm});
            skArc(sketch, "E169", {"start": v(-5.22, 42.22) * mm, "mid": v(-6.37, 42.78) * mm, "end": v(-7.65, 42.87) * mm});
            skArc(sketch, "E170", {"start": v(-2.85, 42.73) * mm, "mid": v(-4.08, 42.68) * mm, "end": v(-5.22, 42.22) * mm});
            skArc(sketch, "E171", {"start": v(-5.22, 41.6) * mm, "mid": v(-6.36, 42.25) * mm, "end": v(-7.65, 42.49) * mm});
            skArc(sketch, "E172", {"start": v(-2.83, 42.17) * mm, "mid": v(-4.07, 42.09) * mm, "end": v(-5.22, 41.6) * mm});
            skLineSegment(sketch, "E173", {"start": v(-7.65, 43.68) * mm, "end": v(-7.65, 43.28) * mm});
            skLineSegment(sketch, "E174", {"start": v(-7.65, 42.87) * mm, "end": v(-7.65, 42.49) * mm});
            skLineSegment(sketch, "E175", {"start": v(-2.83, 42.17) * mm, "end": v(-2.85, 42.73) * mm});
            skLineSegment(sketch, "E176", {"start": v(-2.8, 43.21) * mm, "end": v(-2.82, 43.68) * mm});
            skArc(sketch, "E177", {"start": v(-7.67, 39.9) * mm, "mid": v(-6.34, 40.37) * mm, "end": v(-5.24, 41.25) * mm});
            skArc(sketch, "E178", {"start": v(-5.24, 41.25) * mm, "mid": v(-4.17, 40.34) * mm, "end": v(-2.84, 39.9) * mm});
            skArc(sketch, "E179", {"start": v(-7.67, 39.5) * mm, "mid": v(-6.38, 39.77) * mm, "end": v(-5.24, 40.41) * mm});
            skArc(sketch, "E180", {"start": v(-5.24, 40.41) * mm, "mid": v(-4.1, 39.77) * mm, "end": v(-2.82, 39.44) * mm});
            skArc(sketch, "E181", {"start": v(-5.24, 38.45) * mm, "mid": v(-6.4, 39) * mm, "end": v(-7.67, 39.1) * mm});
            skArc(sketch, "E182", {"start": v(-2.87, 38.95) * mm, "mid": v(-4.1, 38.9) * mm, "end": v(-5.24, 38.45) * mm});
            skArc(sketch, "E183", {"start": v(-5.24, 37.82) * mm, "mid": v(-6.38, 38.47) * mm, "end": v(-7.67, 38.71) * mm});
            skArc(sketch, "E184", {"start": v(-2.85, 38.4) * mm, "mid": v(-4.1, 38.31) * mm, "end": v(-5.24, 37.82) * mm});
            skLineSegment(sketch, "E185", {"start": v(-7.67, 39.9) * mm, "end": v(-7.67, 39.5) * mm});
            skLineSegment(sketch, "E186", {"start": v(-7.67, 39.1) * mm, "end": v(-7.67, 38.71) * mm});
            skLineSegment(sketch, "E187", {"start": v(-2.85, 38.4) * mm, "end": v(-2.87, 38.95) * mm});
            skLineSegment(sketch, "E188", {"start": v(-2.82, 39.44) * mm, "end": v(-2.84, 39.9) * mm});
            skSolve(sketch);
        }
        {
            var Q0;
            Q0=makeQuery(id+"F19.imprint","IMPRINT",FACE,{"disambiguationData":[TD([[makeQuery(id+"F19.imprint","IMPRINT",EDGE,{"derivedFrom":sQuery(id+"F19.wireOp",EDGE,"E105")}),-1.0]])]});
            var Q1;
            Q1=makeQuery(id+"F19.imprint","IMPRINT",FACE,{"disambiguationData":[TD([[makeQuery(id+"F19.imprint","IMPRINT",EDGE,{"derivedFrom":sQuery(id+"F19.wireOp",EDGE,"E109")}),1.0]])]});
            var Q2;
            Q2=makeQuery(id+"F19.imprint","IMPRINT",FACE,{"disambiguationData":[TD([[makeQuery(id+"F19.imprint","IMPRINT",EDGE,{"derivedFrom":sQuery(id+"F19.wireOp",EDGE,"E113")}),-1.0]])]});
            var Q3;
            Q3=makeQuery(id+"F19.imprint","IMPRINT",FACE,{"disambiguationData":[TD([[makeQuery(id+"F19.imprint","IMPRINT",EDGE,{"derivedFrom":sQuery(id+"F19.wireOp",EDGE,"E117")}),1.0]])]});
            extrude(context, id + "F20", {"entities" : qUnion([Q0, Q1, Q2, Q3]), "operationType" : NewBodyOperationType.REMOVE, "oppositeDirection" : true, "depth" : 27.46 * mm, "offsetDistance" : 25.4 * mm});
        }
        {
            var Q0;
            Q0=makeQuery(id+"F19.imprint","IMPRINT",FACE,{"disambiguationData":[TD([[makeQuery(id+"F19.imprint","IMPRINT",EDGE,{"derivedFrom":sQuery(id+"F19.wireOp",EDGE,"E129")}),-1.0]])]});
            var Q1;
            Q1=makeQuery(id+"F19.imprint","IMPRINT",FACE,{"disambiguationData":[TD([[makeQuery(id+"F19.imprint","IMPRINT",EDGE,{"derivedFrom":sQuery(id+"F19.wireOp",EDGE,"E133")}),1.0]])]});
            var Q2;
            Q2=makeQuery(id+"F19.imprint","IMPRINT",FACE,{"disambiguationData":[TD([[makeQuery(id+"F19.imprint","IMPRINT",EDGE,{"derivedFrom":sQuery(id+"F19.wireOp",EDGE,"E141")}),-1.0]])]});
            var Q3;
            Q3=makeQuery(id+"F19.imprint","IMPRINT",FACE,{"disambiguationData":[TD([[makeQuery(id+"F19.imprint","IMPRINT",EDGE,{"derivedFrom":sQuery(id+"F19.wireOp",EDGE,"E145")}),1.0]])]});
            var Q4;
            Q4=makeQuery(id+"F19.imprint","IMPRINT",FACE,{"disambiguationData":[TD([[makeQuery(id+"F19.imprint","IMPRINT",EDGE,{"derivedFrom":sQuery(id+"F19.wireOp",EDGE,"E153")}),-1.0]])]});
            var Q5;
            Q5=makeQuery(id+"F19.imprint","IMPRINT",FACE,{"disambiguationData":[TD([[makeQuery(id+"F19.imprint","IMPRINT",EDGE,{"derivedFrom":sQuery(id+"F19.wireOp",EDGE,"E157")}),1.0]])]});
            var Q6;
            Q6=makeQuery(id+"F19.imprint","IMPRINT",FACE,{"disambiguationData":[TD([[makeQuery(id+"F19.imprint","IMPRINT",EDGE,{"derivedFrom":sQuery(id+"F19.wireOp",EDGE,"E165")}),-1.0]])]});
            var Q7;
            Q7=makeQuery(id+"F19.imprint","IMPRINT",FACE,{"disambiguationData":[TD([[makeQuery(id+"F19.imprint","IMPRINT",EDGE,{"derivedFrom":sQuery(id+"F19.wireOp",EDGE,"E169")}),1.0]])]});
            var Q8;
            Q8=makeQuery(id+"F19.imprint","IMPRINT",FACE,{"disambiguationData":[TD([[makeQuery(id+"F19.imprint","IMPRINT",EDGE,{"derivedFrom":sQuery(id+"F19.wireOp",EDGE,"E177")}),-1.0]])]});
            var Q9;
            Q9=makeQuery(id+"F19.imprint","IMPRINT",FACE,{"disambiguationData":[TD([[makeQuery(id+"F19.imprint","IMPRINT",EDGE,{"derivedFrom":sQuery(id+"F19.wireOp",EDGE,"E181")}),1.0]])]});
            extrude(context, id + "F21", {"entities" : qUnion([Q0, Q1, Q2, Q3, Q4, Q5, Q6, Q7, Q8, Q9]), "operationType" : NewBodyOperationType.REMOVE, "oppositeDirection" : true, "depth" : 33.78 * mm, "offsetDistance" : 25.4 * mm});
        }
        {
            var Q0;
            Q0=qCreatedBy(makeId("Top.planeOp"),FACE);
            var sketch = newSketch(context, id + "F22", { "sketchPlane" : qUnion([Q0])});
            skLineSegment(sketch, "E189", {"start": v(-7.61, 54.25) * mm, "end": v(-7.61, 54.64) * mm});
            skArc(sketch, "E190", {"start": v(-7.67, 39.88) * mm, "mid": v(-6.34, 40.34) * mm, "end": v(-5.24, 41.23) * mm});
            skArc(sketch, "E191", {"start": v(-5.24, 41.23) * mm, "mid": v(-4.18, 40.32) * mm, "end": v(-2.85, 39.88) * mm});
            skArc(sketch, "E192", {"start": v(-7.67, 39.48) * mm, "mid": v(-6.39, 39.75) * mm, "end": v(-5.24, 40.39) * mm});
            skArc(sketch, "E193", {"start": v(-5.24, 40.39) * mm, "mid": v(-4.1, 39.75) * mm, "end": v(-2.82, 39.41) * mm});
            skArc(sketch, "E194", {"start": v(-5.24, 38.42) * mm, "mid": v(-6.4, 38.98) * mm, "end": v(-7.67, 39.07) * mm});
            skArc(sketch, "E195", {"start": v(-2.88, 38.93) * mm, "mid": v(-4.1, 38.88) * mm, "end": v(-5.24, 38.42) * mm});
            skArc(sketch, "E196", {"start": v(-5.24, 37.8) * mm, "mid": v(-6.39, 38.44) * mm, "end": v(-7.67, 38.69) * mm});
            skArc(sketch, "E197", {"start": v(-2.85, 38.37) * mm, "mid": v(-4.1, 38.29) * mm, "end": v(-5.24, 37.8) * mm});
            skLineSegment(sketch, "E198", {"start": v(-7.67, 39.88) * mm, "end": v(-7.67, 39.48) * mm});
            skLineSegment(sketch, "E199", {"start": v(-7.67, 39.07) * mm, "end": v(-7.67, 38.69) * mm});
            skLineSegment(sketch, "E200", {"start": v(-2.85, 38.37) * mm, "end": v(-2.88, 38.93) * mm});
            skLineSegment(sketch, "E201", {"start": v(-2.82, 39.41) * mm, "end": v(-2.85, 39.88) * mm});
            skArc(sketch, "E202", {"start": v(-7.58, 43.67) * mm, "mid": v(-6.25, 44.14) * mm, "end": v(-5.15, 45.02) * mm});
            skArc(sketch, "E203", {"start": v(-5.15, 45.02) * mm, "mid": v(-4.08, 44.11) * mm, "end": v(-2.75, 43.67) * mm});
            skArc(sketch, "E204", {"start": v(-7.58, 43.28) * mm, "mid": v(-6.3, 43.54) * mm, "end": v(-5.15, 44.19) * mm});
            skArc(sketch, "E205", {"start": v(-5.15, 44.19) * mm, "mid": v(-4, 43.54) * mm, "end": v(-2.73, 43.2) * mm});
            skArc(sketch, "E206", {"start": v(-5.15, 42.22) * mm, "mid": v(-6.3, 42.78) * mm, "end": v(-7.58, 42.87) * mm});
            skArc(sketch, "E207", {"start": v(-2.78, 42.72) * mm, "mid": v(-4, 42.67) * mm, "end": v(-5.15, 42.22) * mm});
            skArc(sketch, "E208", {"start": v(-5.15, 41.6) * mm, "mid": v(-6.29, 42.24) * mm, "end": v(-7.58, 42.48) * mm});
            skArc(sketch, "E209", {"start": v(-2.76, 42.17) * mm, "mid": v(-4, 42.08) * mm, "end": v(-5.15, 41.6) * mm});
            skLineSegment(sketch, "E210", {"start": v(-7.58, 43.67) * mm, "end": v(-7.58, 43.28) * mm});
            skLineSegment(sketch, "E211", {"start": v(-7.58, 42.87) * mm, "end": v(-7.58, 42.48) * mm});
            skLineSegment(sketch, "E212", {"start": v(-2.76, 42.17) * mm, "end": v(-2.78, 42.72) * mm});
            skLineSegment(sketch, "E213", {"start": v(-2.73, 43.2) * mm, "end": v(-2.75, 43.67) * mm});
            skArc(sketch, "E214", {"start": v(-7.7, 47.79) * mm, "mid": v(-6.38, 48.25) * mm, "end": v(-5.28, 49.14) * mm});
            skArc(sketch, "E215", {"start": v(-5.28, 49.14) * mm, "mid": v(-4.21, 48.22) * mm, "end": v(-2.88, 47.79) * mm});
            skArc(sketch, "E216", {"start": v(-7.7, 47.39) * mm, "mid": v(-6.42, 47.65) * mm, "end": v(-5.28, 48.3) * mm});
            skArc(sketch, "E217", {"start": v(-5.28, 48.3) * mm, "mid": v(-4.13, 47.65) * mm, "end": v(-2.86, 47.32) * mm});
            skArc(sketch, "E218", {"start": v(-5.28, 46.33) * mm, "mid": v(-6.43, 46.9) * mm, "end": v(-7.7, 46.98) * mm});
            skArc(sketch, "E219", {"start": v(-2.91, 46.84) * mm, "mid": v(-4.14, 46.78) * mm, "end": v(-5.28, 46.33) * mm});
            skArc(sketch, "E220", {"start": v(-5.28, 45.7) * mm, "mid": v(-6.42, 46.35) * mm, "end": v(-7.7, 46.6) * mm});
            skArc(sketch, "E221", {"start": v(-2.89, 46.28) * mm, "mid": v(-4.13, 46.2) * mm, "end": v(-5.28, 45.7) * mm});
            skLineSegment(sketch, "E222", {"start": v(-7.7, 47.79) * mm, "end": v(-7.7, 47.39) * mm});
            skLineSegment(sketch, "E223", {"start": v(-7.7, 46.98) * mm, "end": v(-7.7, 46.6) * mm});
            skLineSegment(sketch, "E224", {"start": v(-2.89, 46.28) * mm, "end": v(-2.91, 46.84) * mm});
            skLineSegment(sketch, "E225", {"start": v(-2.86, 47.32) * mm, "end": v(-2.88, 47.79) * mm});
            skArc(sketch, "E226", {"start": v(-7.5, 51.64) * mm, "mid": v(-6.18, 52.1) * mm, "end": v(-5.08, 53) * mm});
            skArc(sketch, "E227", {"start": v(-5.08, 53) * mm, "mid": v(-4.01, 52.08) * mm, "end": v(-2.68, 51.64) * mm});
            skArc(sketch, "E228", {"start": v(-7.5, 51.25) * mm, "mid": v(-6.22, 51.51) * mm, "end": v(-5.08, 52.15) * mm});
            skArc(sketch, "E229", {"start": v(-5.08, 52.15) * mm, "mid": v(-3.93, 51.51) * mm, "end": v(-2.66, 51.18) * mm});
            skArc(sketch, "E230", {"start": v(-5.08, 50.19) * mm, "mid": v(-6.23, 50.75) * mm, "end": v(-7.5, 50.83) * mm});
            skArc(sketch, "E231", {"start": v(-2.71, 50.7) * mm, "mid": v(-3.94, 50.64) * mm, "end": v(-5.08, 50.19) * mm});
            skArc(sketch, "E232", {"start": v(-5.08, 49.56) * mm, "mid": v(-6.22, 50.2) * mm, "end": v(-7.5, 50.45) * mm});
            skArc(sketch, "E233", {"start": v(-2.69, 50.14) * mm, "mid": v(-3.93, 50.05) * mm, "end": v(-5.08, 49.56) * mm});
            skLineSegment(sketch, "E234", {"start": v(-7.5, 51.64) * mm, "end": v(-7.5, 51.25) * mm});
            skLineSegment(sketch, "E235", {"start": v(-7.5, 50.83) * mm, "end": v(-7.5, 50.45) * mm});
            skLineSegment(sketch, "E236", {"start": v(-2.69, 50.14) * mm, "end": v(-2.71, 50.7) * mm});
            skLineSegment(sketch, "E237", {"start": v(-2.66, 51.18) * mm, "end": v(-2.68, 51.64) * mm});
            skArc(sketch, "E238", {"start": v(-7.63, 55.46) * mm, "mid": v(-6.3, 55.92) * mm, "end": v(-5.2, 56.8) * mm});
            skArc(sketch, "E239", {"start": v(-5.2, 56.8) * mm, "mid": v(-4.13, 55.9) * mm, "end": v(-2.8, 55.46) * mm});
            skArc(sketch, "E240", {"start": v(-7.63, 55.06) * mm, "mid": v(-6.34, 55.33) * mm, "end": v(-5.2, 55.97) * mm});
            skArc(sketch, "E241", {"start": v(-5.2, 55.97) * mm, "mid": v(-4.05, 55.33) * mm, "end": v(-2.78, 55) * mm});
            skArc(sketch, "E242", {"start": v(-5.2, 54) * mm, "mid": v(-6.35, 54.56) * mm, "end": v(-7.63, 54.65) * mm});
            skArc(sketch, "E243", {"start": v(-2.83, 54.5) * mm, "mid": v(-4.06, 54.46) * mm, "end": v(-5.2, 54) * mm});
            skArc(sketch, "E244", {"start": v(-5.2, 53.38) * mm, "mid": v(-6.34, 54.02) * mm, "end": v(-7.63, 54.27) * mm});
            skArc(sketch, "E245", {"start": v(-2.8, 53.95) * mm, "mid": v(-4.05, 53.87) * mm, "end": v(-5.2, 53.38) * mm});
            skLineSegment(sketch, "E246", {"start": v(-7.63, 55.46) * mm, "end": v(-7.63, 55.06) * mm});
            skLineSegment(sketch, "E247", {"start": v(-7.63, 54.65) * mm, "end": v(-7.63, 54.27) * mm});
            skLineSegment(sketch, "E248", {"start": v(-2.8, 53.95) * mm, "end": v(-2.83, 54.5) * mm});
            skLineSegment(sketch, "E249", {"start": v(-2.78, 55) * mm, "end": v(-2.8, 55.46) * mm});
            skArc(sketch, "E250", {"start": v(-7.6, 59) * mm, "mid": v(-6.28, 59.47) * mm, "end": v(-5.18, 60.36) * mm});
            skArc(sketch, "E251", {"start": v(-5.18, 60.36) * mm, "mid": v(-4.11, 59.45) * mm, "end": v(-2.78, 59) * mm});
            skArc(sketch, "E252", {"start": v(-7.6, 58.61) * mm, "mid": v(-6.32, 58.88) * mm, "end": v(-5.18, 59.52) * mm});
            skArc(sketch, "E253", {"start": v(-5.18, 59.52) * mm, "mid": v(-4.03, 58.88) * mm, "end": v(-2.76, 58.54) * mm});
            skArc(sketch, "E254", {"start": v(-5.18, 57.55) * mm, "mid": v(-6.33, 58.11) * mm, "end": v(-7.6, 58.2) * mm});
            skArc(sketch, "E255", {"start": v(-2.81, 58.06) * mm, "mid": v(-4.04, 58) * mm, "end": v(-5.18, 57.55) * mm});
            skArc(sketch, "E256", {"start": v(-5.18, 56.93) * mm, "mid": v(-6.32, 57.57) * mm, "end": v(-7.6, 57.82) * mm});
            skArc(sketch, "E257", {"start": v(-2.79, 57.5) * mm, "mid": v(-4.03, 57.42) * mm, "end": v(-5.18, 56.93) * mm});
            skLineSegment(sketch, "E258", {"start": v(-7.6, 59) * mm, "end": v(-7.6, 58.61) * mm});
            skLineSegment(sketch, "E259", {"start": v(-7.6, 58.2) * mm, "end": v(-7.6, 57.82) * mm});
            skLineSegment(sketch, "E260", {"start": v(-2.79, 57.5) * mm, "end": v(-2.81, 58.06) * mm});
            skLineSegment(sketch, "E261", {"start": v(-2.76, 58.54) * mm, "end": v(-2.78, 59) * mm});
            skLineSegment(sketch, "E262", {"start": v(-7.6, 61.22) * mm, "end": v(-7.6, 61.74) * mm});
            skLineSegment(sketch, "E263", {"start": v(-2.88, 61.12) * mm, "end": v(-2.88, 61.6) * mm});
            skArc(sketch, "E264", {"start": v(-5.28, 61.17) * mm, "mid": v(-6.41, 61.57) * mm, "end": v(-7.6, 61.74) * mm});
            skArc(sketch, "E265", {"start": v(-2.88, 61.6) * mm, "mid": v(-4.12, 61.58) * mm, "end": v(-5.28, 61.17) * mm});
            skArc(sketch, "E266", {"start": v(-5.28, 60.72) * mm, "mid": v(-6.4, 61.15) * mm, "end": v(-7.6, 61.22) * mm});
            skArc(sketch, "E267", {"start": v(-2.88, 61.12) * mm, "mid": v(-4.1, 61.02) * mm, "end": v(-5.28, 60.72) * mm});
            skArc(sketch, "E268", {"start": v(-7.6, 62.17) * mm, "mid": v(-6.3, 62.65) * mm, "end": v(-5.28, 63.58) * mm});
            skArc(sketch, "E269", {"start": v(-5.28, 63.58) * mm, "mid": v(-4.21, 62.66) * mm, "end": v(-2.88, 62.22) * mm});
            skArc(sketch, "E270", {"start": v(-7.6, 62.72) * mm, "mid": v(-6.22, 63.32) * mm, "end": v(-5.28, 64.5) * mm});
            skArc(sketch, "E271", {"start": v(-5.28, 64.5) * mm, "mid": v(-4.33, 63.3) * mm, "end": v(-2.88, 62.84) * mm});
            skLineSegment(sketch, "E272", {"start": v(-7.6, 62.17) * mm, "end": v(-7.6, 62.72) * mm});
            skLineSegment(sketch, "E273", {"start": v(-2.88, 62.84) * mm, "end": v(-2.88, 62.22) * mm});
            skSolve(sketch);
        }
        {
            var Q0;
            Q0=qSketchRegion(id+"F22",true);
            extrude(context, id + "F23", {"entities" : qUnion([Q0]), "endBound" : BoundingType.SYMMETRIC, "depth" : 3.96 * mm, "offsetDistance" : 25.4 * mm});
        }
        {
            var Q0;
            Q0=makeQuery(id+"F23.opExtrude","CAP_EDGE",EDGE,{"disambiguationData":[OSD([sQuery(id+"F22.wireOp",EDGE,"E198")])],"isStart":true});
            var Q1;
            Q1=makeQuery(id+"F23.opExtrude","CAP_EDGE",EDGE,{"disambiguationData":[OSD([sQuery(id+"F22.wireOp",EDGE,"E199")])],"isStart":true});
            var Q2;
            Q2=makeQuery(id+"F23.opExtrude","CAP_EDGE",EDGE,{"disambiguationData":[OSD([sQuery(id+"F22.wireOp",EDGE,"E200")])],"isStart":true});
            var Q3;
            Q3=makeQuery(id+"F23.opExtrude","CAP_EDGE",EDGE,{"disambiguationData":[OSD([sQuery(id+"F22.wireOp",EDGE,"E201")])],"isStart":true});
            var Q4;
            Q4=makeQuery(id+"F23.opExtrude","CAP_EDGE",EDGE,{"disambiguationData":[OSD([sQuery(id+"F22.wireOp",EDGE,"E200")])],"isStart":false});
            var Q5;
            Q5=makeQuery(id+"F23.opExtrude","CAP_EDGE",EDGE,{"disambiguationData":[OSD([sQuery(id+"F22.wireOp",EDGE,"E201")])],"isStart":false});
            var Q6;
            Q6=makeQuery(id+"F23.opExtrude","CAP_EDGE",EDGE,{"disambiguationData":[OSD([sQuery(id+"F22.wireOp",EDGE,"E198")])],"isStart":false});
            var Q7;
            Q7=makeQuery(id+"F23.opExtrude","CAP_EDGE",EDGE,{"disambiguationData":[OSD([sQuery(id+"F22.wireOp",EDGE,"E199")])],"isStart":false});
            var Q8;
            Q8=makeQuery(id+"F23.opExtrude","CAP_EDGE",EDGE,{"disambiguationData":[OSD([sQuery(id+"F22.wireOp",EDGE,"E212")])],"isStart":false});
            var Q9;
            Q9=makeQuery(id+"F23.opExtrude","CAP_EDGE",EDGE,{"disambiguationData":[OSD([sQuery(id+"F22.wireOp",EDGE,"E211")])],"isStart":false});
            var Q10;
            Q10=makeQuery(id+"F23.opExtrude","CAP_EDGE",EDGE,{"disambiguationData":[OSD([sQuery(id+"F22.wireOp",EDGE,"E213")])],"isStart":false});
            var Q11;
            Q11=makeQuery(id+"F23.opExtrude","CAP_EDGE",EDGE,{"disambiguationData":[OSD([sQuery(id+"F22.wireOp",EDGE,"E210")])],"isStart":false});
            var Q12;
            Q12=makeQuery(id+"F23.opExtrude","CAP_EDGE",EDGE,{"disambiguationData":[OSD([sQuery(id+"F22.wireOp",EDGE,"E211")])],"isStart":true});
            var Q13;
            Q13=makeQuery(id+"F23.opExtrude","CAP_EDGE",EDGE,{"disambiguationData":[OSD([sQuery(id+"F22.wireOp",EDGE,"E212")])],"isStart":true});
            var Q14;
            Q14=makeQuery(id+"F23.opExtrude","CAP_EDGE",EDGE,{"disambiguationData":[OSD([sQuery(id+"F22.wireOp",EDGE,"E213")])],"isStart":true});
            var Q15;
            Q15=makeQuery(id+"F23.opExtrude","CAP_EDGE",EDGE,{"disambiguationData":[OSD([sQuery(id+"F22.wireOp",EDGE,"E210")])],"isStart":true});
            var Q16;
            Q16=makeQuery(id+"F23.opExtrude","CAP_EDGE",EDGE,{"disambiguationData":[OSD([sQuery(id+"F22.wireOp",EDGE,"E224")])],"isStart":false});
            var Q17;
            Q17=makeQuery(id+"F23.opExtrude","CAP_EDGE",EDGE,{"disambiguationData":[OSD([sQuery(id+"F22.wireOp",EDGE,"E224")])],"isStart":true});
            var Q18;
            Q18=makeQuery(id+"F23.opExtrude","CAP_EDGE",EDGE,{"disambiguationData":[OSD([sQuery(id+"F22.wireOp",EDGE,"E223")])],"isStart":false});
            var Q19;
            Q19=makeQuery(id+"F23.opExtrude","CAP_EDGE",EDGE,{"disambiguationData":[OSD([sQuery(id+"F22.wireOp",EDGE,"E223")])],"isStart":true});
            var Q20;
            Q20=makeQuery(id+"F23.opExtrude","CAP_EDGE",EDGE,{"disambiguationData":[OSD([sQuery(id+"F22.wireOp",EDGE,"E225")])],"isStart":true});
            var Q21;
            Q21=makeQuery(id+"F23.opExtrude","CAP_EDGE",EDGE,{"disambiguationData":[OSD([sQuery(id+"F22.wireOp",EDGE,"E225")])],"isStart":false});
            var Q22;
            Q22=makeQuery(id+"F23.opExtrude","CAP_EDGE",EDGE,{"disambiguationData":[OSD([sQuery(id+"F22.wireOp",EDGE,"E222")])],"isStart":true});
            var Q23;
            Q23=makeQuery(id+"F23.opExtrude","CAP_EDGE",EDGE,{"disambiguationData":[OSD([sQuery(id+"F22.wireOp",EDGE,"E222")])],"isStart":false});
            var Q24;
            Q24=makeQuery(id+"F23.opExtrude","CAP_EDGE",EDGE,{"disambiguationData":[OSD([sQuery(id+"F22.wireOp",EDGE,"E235")])],"isStart":true});
            var Q25;
            Q25=makeQuery(id+"F23.opExtrude","CAP_EDGE",EDGE,{"disambiguationData":[OSD([sQuery(id+"F22.wireOp",EDGE,"E236")])],"isStart":true});
            var Q26;
            Q26=makeQuery(id+"F23.opExtrude","CAP_EDGE",EDGE,{"disambiguationData":[OSD([sQuery(id+"F22.wireOp",EDGE,"E234")])],"isStart":true});
            var Q27;
            Q27=makeQuery(id+"F23.opExtrude","CAP_EDGE",EDGE,{"disambiguationData":[OSD([sQuery(id+"F22.wireOp",EDGE,"E237")])],"isStart":true});
            var Q28;
            Q28=makeQuery(id+"F23.opExtrude","CAP_EDGE",EDGE,{"disambiguationData":[OSD([sQuery(id+"F22.wireOp",EDGE,"E235")])],"isStart":false});
            var Q29;
            Q29=makeQuery(id+"F23.opExtrude","CAP_EDGE",EDGE,{"disambiguationData":[OSD([sQuery(id+"F22.wireOp",EDGE,"E234")])],"isStart":false});
            var Q30;
            Q30=makeQuery(id+"F23.opExtrude","CAP_EDGE",EDGE,{"disambiguationData":[OSD([sQuery(id+"F22.wireOp",EDGE,"E236")])],"isStart":false});
            var Q31;
            Q31=makeQuery(id+"F23.opExtrude","CAP_EDGE",EDGE,{"disambiguationData":[OSD([sQuery(id+"F22.wireOp",EDGE,"E237")])],"isStart":false});
            var Q32;
            Q32=makeQuery(id+"F23.opExtrude","CAP_EDGE",EDGE,{"disambiguationData":[OSD([sQuery(id+"F22.wireOp",EDGE,"E247")])],"isStart":false});
            var Q33;
            Q33=makeQuery(id+"F23.opExtrude","CAP_EDGE",EDGE,{"disambiguationData":[OSD([sQuery(id+"F22.wireOp",EDGE,"E248")])],"isStart":false});
            var Q34;
            Q34=makeQuery(id+"F23.opExtrude","CAP_EDGE",EDGE,{"disambiguationData":[OSD([sQuery(id+"F22.wireOp",EDGE,"E248")])],"isStart":true});
            var Q35;
            Q35=makeQuery(id+"F23.opExtrude","CAP_EDGE",EDGE,{"disambiguationData":[OSD([sQuery(id+"F22.wireOp",EDGE,"E247")])],"isStart":true});
            var Q36;
            Q36=makeQuery(id+"F23.opExtrude","CAP_EDGE",EDGE,{"disambiguationData":[OSD([sQuery(id+"F22.wireOp",EDGE,"E246")])],"isStart":true});
            var Q37;
            Q37=makeQuery(id+"F23.opExtrude","CAP_EDGE",EDGE,{"disambiguationData":[OSD([sQuery(id+"F22.wireOp",EDGE,"E246")])],"isStart":false});
            var Q38;
            Q38=makeQuery(id+"F23.opExtrude","CAP_EDGE",EDGE,{"disambiguationData":[OSD([sQuery(id+"F22.wireOp",EDGE,"E249")])],"isStart":true});
            var Q39;
            Q39=makeQuery(id+"F23.opExtrude","CAP_EDGE",EDGE,{"disambiguationData":[OSD([sQuery(id+"F22.wireOp",EDGE,"E249")])],"isStart":false});
            var Q40;
            Q40=makeQuery(id+"F23.opExtrude","CAP_EDGE",EDGE,{"disambiguationData":[OSD([sQuery(id+"F22.wireOp",EDGE,"E260")])],"isStart":false});
            var Q41;
            Q41=makeQuery(id+"F23.opExtrude","CAP_EDGE",EDGE,{"disambiguationData":[OSD([sQuery(id+"F22.wireOp",EDGE,"E260")])],"isStart":true});
            var Q42;
            Q42=makeQuery(id+"F23.opExtrude","CAP_EDGE",EDGE,{"disambiguationData":[OSD([sQuery(id+"F22.wireOp",EDGE,"E259")])],"isStart":true});
            var Q43;
            Q43=makeQuery(id+"F23.opExtrude","CAP_EDGE",EDGE,{"disambiguationData":[OSD([sQuery(id+"F22.wireOp",EDGE,"E259")])],"isStart":false});
            var Q44;
            Q44=makeQuery(id+"F23.opExtrude","CAP_EDGE",EDGE,{"disambiguationData":[OSD([sQuery(id+"F22.wireOp",EDGE,"E258")])],"isStart":false});
            var Q45;
            Q45=makeQuery(id+"F23.opExtrude","CAP_EDGE",EDGE,{"disambiguationData":[OSD([sQuery(id+"F22.wireOp",EDGE,"E258")])],"isStart":true});
            var Q46;
            Q46=makeQuery(id+"F23.opExtrude","CAP_EDGE",EDGE,{"disambiguationData":[OSD([sQuery(id+"F22.wireOp",EDGE,"E261")])],"isStart":false});
            var Q47;
            Q47=makeQuery(id+"F23.opExtrude","CAP_EDGE",EDGE,{"disambiguationData":[OSD([sQuery(id+"F22.wireOp",EDGE,"E261")])],"isStart":true});
            var Q48;
            Q48=makeQuery(id+"F23.opExtrude","CAP_EDGE",EDGE,{"disambiguationData":[OSD([sQuery(id+"F22.wireOp",EDGE,"E263")])],"isStart":false});
            var Q49;
            Q49=makeQuery(id+"F23.opExtrude","CAP_EDGE",EDGE,{"disambiguationData":[OSD([sQuery(id+"F22.wireOp",EDGE,"E263")])],"isStart":true});
            var Q50;
            Q50=makeQuery(id+"F23.opExtrude","CAP_EDGE",EDGE,{"disambiguationData":[OSD([sQuery(id+"F22.wireOp",EDGE,"E262")])],"isStart":false});
            var Q51;
            Q51=makeQuery(id+"F23.opExtrude","CAP_EDGE",EDGE,{"disambiguationData":[OSD([sQuery(id+"F22.wireOp",EDGE,"E262")])],"isStart":true});
            var Q52;
            Q52=makeQuery(id+"F23.opExtrude","CAP_EDGE",EDGE,{"disambiguationData":[OSD([sQuery(id+"F22.wireOp",EDGE,"E272")])],"isStart":true});
            var Q53;
            Q53=makeQuery(id+"F23.opExtrude","CAP_EDGE",EDGE,{"disambiguationData":[OSD([sQuery(id+"F22.wireOp",EDGE,"E272")])],"isStart":false});
            var Q54;
            Q54=makeQuery(id+"F23.opExtrude","CAP_EDGE",EDGE,{"disambiguationData":[OSD([sQuery(id+"F22.wireOp",EDGE,"E273")])],"isStart":true});
            var Q55;
            Q55=makeQuery(id+"F23.opExtrude","CAP_EDGE",EDGE,{"disambiguationData":[OSD([sQuery(id+"F22.wireOp",EDGE,"E273")])],"isStart":false});
            fillet(context, id + "F24", {"entities" : qUnion([Q0, Q1, Q2, Q3, Q4, Q5, Q6, Q7, Q8, Q9, Q10, Q11, Q12, Q13, Q14, Q15, Q16, Q17, Q18, Q19, Q20, Q21, Q22, Q23, Q24, Q25, Q26, Q27, Q28, Q29, Q30, Q31, Q32, Q33, Q34, Q35, Q36, Q37, Q38, Q39, Q40, Q41, Q42, Q43, Q44, Q45, Q46, Q47, Q48, Q49, Q50, Q51, Q52, Q53, Q54, Q55]), "radius" : 3.07 * mm, "tangentPropagation" : true, "allowEdgeOverflow" : false});
        }
        {
            var Q0;
            Q0=makeQuery(id+"F14.opExtrude","CAP_FACE",FACE,{"disambiguationData":[OSD([sQuery(id+"F0.wireOp",EDGE,"E66"),sQuery(id+"F0.wireOp",EDGE,"E67"),sQuery(id+"F0.wireOp",EDGE,"E76"),sQuery(id+"F0.wireOp",EDGE,"E79"),sQuery(id+"F0.wireOp",EDGE,"E80"),sQuery(id+"F0.wireOp",EDGE,"E81"),sQuery(id+"F0.wireOp",EDGE,"E82"),sQuery(id+"F0.wireOp",EDGE,"E83"),sQuery(id+"F0.wireOp",EDGE,"E90"),sQuery(id+"F0.wireOp",EDGE,"E91"),sQuery(id+"F0.wireOp",EDGE,"E92"),sQuery(id+"F0.wireOp",EDGE,"E93"),sQuery(id+"F0.wireOp",EDGE,"E94"),sQuery(id+"F0.wireOp",EDGE,"E95.MirrorCS"),sQuery(id+"F0.wireOp",EDGE,"E96.MirrorCS"),sQuery(id+"F0.wireOp",EDGE,"E97.MirrorCS"),sQuery(id+"F0.wireOp",EDGE,"E98.MirrorCS"),sQuery(id+"F0.wireOp",EDGE,"E99.MirrorCS"),sQuery(id+"F0.wireOp",EDGE,"E100"),sQuery(id+"F0.wireOp",EDGE,"E101"),sQuery(id+"F0.wireOp",EDGE,"E102"),sQuery(id+"F0.wireOp",EDGE,"E103"),sQuery(id+"F0.wireOp",EDGE,"E104")])],"isStart":false});
            var sketch = newSketch(context, id + "F25", { "sketchPlane" : qUnion([Q0])});
            skLineSegment(sketch, "E274", {"start": v(-8.92, 3.9) * mm, "end": v(-7.08, 0.66) * mm});
            skLineSegment(sketch, "E275", {"start": v(-7.08, 0.66) * mm, "end": v(-5.26, 3.86) * mm});
            skLineSegment(sketch, "E276", {"start": v(-5.26, 3.86) * mm, "end": v(-8.92, 3.9) * mm});
            skLineSegment(sketch, "E277", {"start": v(-5.14, 3.86) * mm, "end": v(-3.3, 0.61) * mm});
            skLineSegment(sketch, "E278", {"start": v(-3.3, 0.61) * mm, "end": v(-1.4, 3.9) * mm});
            skLineSegment(sketch, "E279", {"start": v(-1.4, 3.9) * mm, "end": v(-5.14, 3.86) * mm});
            skLineSegment(sketch, "E280", {"start": v(-7.08, 0.58) * mm, "end": v(-3.35, 0.58) * mm});
            skLineSegment(sketch, "E281", {"start": v(-3.35, 0.58) * mm, "end": v(-5.13, -2.57) * mm});
            skLineSegment(sketch, "E282", {"start": v(-5.13, -2.57) * mm, "end": v(-7.08, 0.58) * mm});
            skSolve(sketch);
        }
        {
            var Q0;
            Q0=makeQuery(id+"F25.imprint","IMPRINT",FACE,{"disambiguationData":[TD([[makeQuery(id+"F25.imprint","IMPRINT",EDGE,{"derivedFrom":sQuery(id+"F25.wireOp",EDGE,"E274")}),1.0]])]});
            var Q1;
            Q1=makeQuery(id+"F25.imprint","IMPRINT",FACE,{"disambiguationData":[TD([[makeQuery(id+"F25.imprint","IMPRINT",EDGE,{"derivedFrom":sQuery(id+"F25.wireOp",EDGE,"E277")}),1.0]])]});
            var Q2;
            Q2=makeQuery(id+"F25.imprint","IMPRINT",FACE,{"disambiguationData":[TD([[makeQuery(id+"F25.imprint","IMPRINT",EDGE,{"derivedFrom":sQuery(id+"F25.wireOp",EDGE,"E280")}),-1.0]])]});
            extrude(context, id + "F26", {"entities" : qUnion([Q0, Q1, Q2]), "operationType" : NewBodyOperationType.ADD, "depth" : 0.33 * mm, "offsetDistance" : 25.4 * mm});
        }
    });
